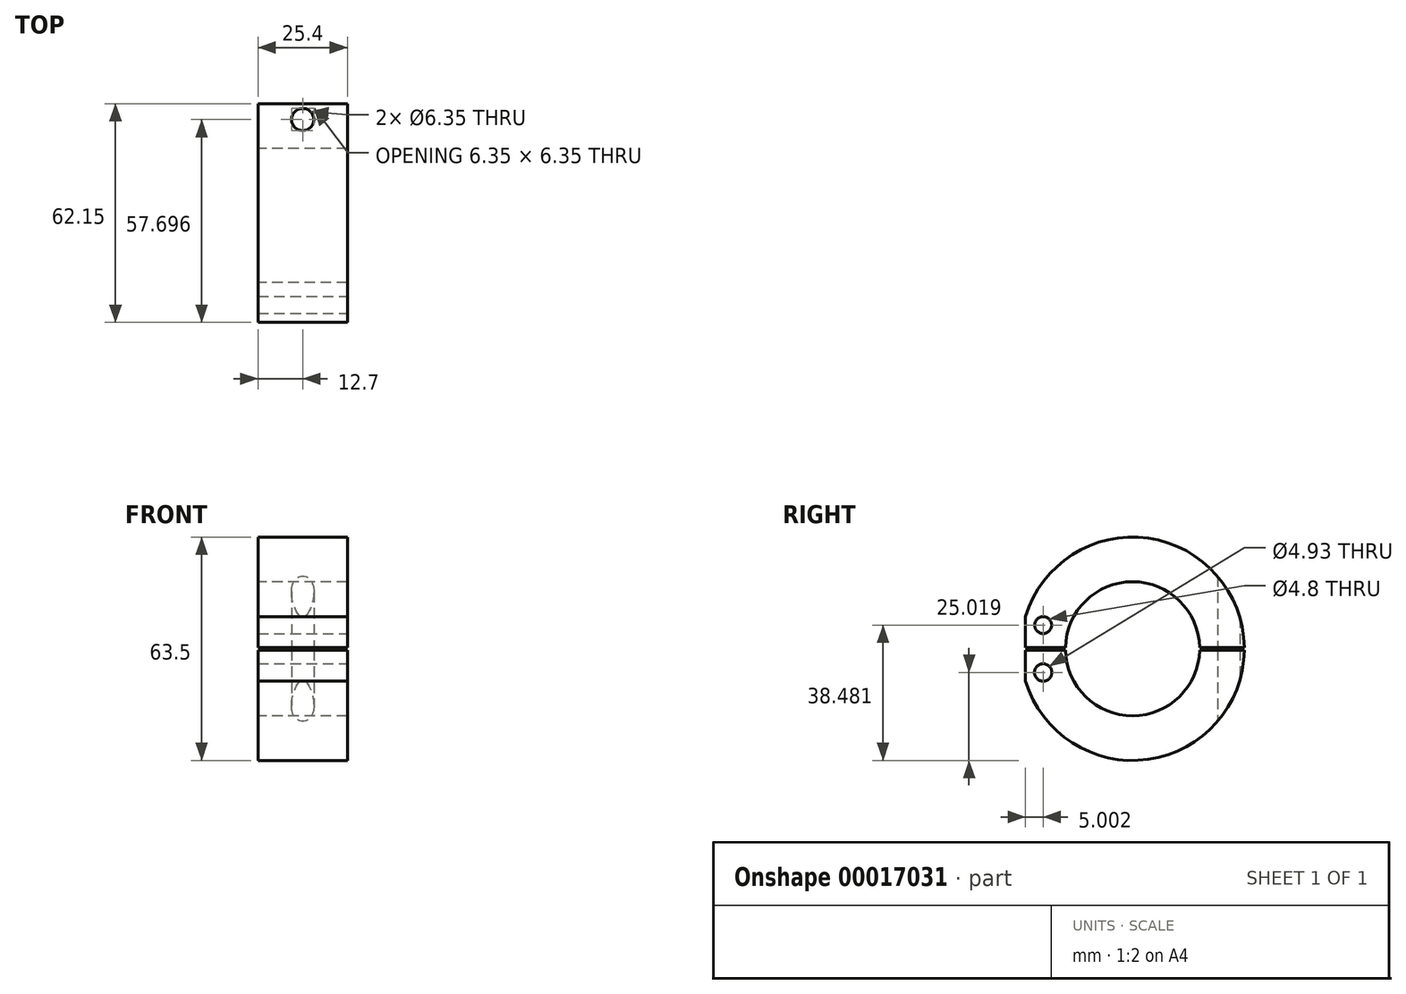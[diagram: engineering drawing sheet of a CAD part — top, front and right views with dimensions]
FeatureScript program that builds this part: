
annotation { "Feature Type Name" : "Feature", "Feature Type Description" : "" }
export const myFeature = defineFeature(function(context is Context, id is Id, definition is map)
    precondition{}
    {
        {
            var Q0;
            Q0=qCreatedBy(makeId("Right.planeOp"),FACE);
            var sketch = newSketch(context, id + "F0", { "sketchPlane" : qUnion([Q0])});
            skArc(sketch, "E0", {"start": v(-19.05, -0.38) * mm, "mid": v(0, -19.05) * mm, "end": v(19.05, -0.38) * mm});
            skArc(sketch, "E1", {"start": v(-31.75, -0.38) * mm, "mid": v(0, -31.75) * mm, "end": v(31.75, -0.38) * mm});
            skLineSegment(sketch, "E2.0", {"start": v(-31.75, 0.38) * mm, "end": v(-19.05, 0.38) * mm});
            skLineSegment(sketch, "E3.0", {"start": v(-31.75, -0.38) * mm, "end": v(-19.05, -0.38) * mm});
            skLineSegment(sketch, "E4.trimOffspring", {"start": v(19.05, 0.38) * mm, "end": v(31.75, 0.38) * mm});
            skArc(sketch, "E5.trimOffspring", {"start": v(19.05, 0.38) * mm, "mid": v(0, 19.05) * mm, "end": v(-19.05, 0.38) * mm});
            skArc(sketch, "E6.trimOffspring", {"start": v(31.75, 0.38) * mm, "mid": v(0, 31.75) * mm, "end": v(-31.75, 0.38) * mm});
            skLineSegment(sketch, "E7.trimOffspring", {"start": v(19.05, -0.38) * mm, "end": v(31.75, -0.38) * mm});
            skSolve(sketch);
        }
        {
            var Q0;
            Q0 = qSketchRegion(id + "F0", true);
            extrude(context, id + "F1", {"entities" : qUnion([Q0]), "depth" : 12.7 * mm, "hasSecondDirection" : true, "secondDirectionOppositeDirection" : true, "secondDirectionDepth" : 12.7 * mm});
        }
        {
            var Q0;
            Q0=qCreatedBy(makeId("Top.planeOp"),FACE);
            var sketch = newSketch(context, id + "F2", { "sketchPlane" : qUnion([Q0])});
            skCircle(sketch, "E8", {"center": v(0, 27.3) * mm, "radius": 3.18 * mm});
            skSolve(sketch);
        }
        {
            var Q0;
            Q0 = qSketchRegion(id + "F2", true);
            extrude(context, id + "F3", {"entities" : qUnion([Q0]), "operationType" : NewBodyOperationType.REMOVE, "depth" : 43.87 * mm, "hasSecondDirection" : true, "secondDirectionOppositeDirection" : true, "secondDirectionDepth" : 40.07 * mm});
        }
        {
            var Q0;
            Q0=makeQuery(id+"F1.opExtrude","CAP_FACE",FACE,{"disambiguationData":[OSD([sQuery(id+"F0.wireOp",EDGE,"E2.0"),sQuery(id+"F0.wireOp",EDGE,"E4.trimOffspring"),sQuery(id+"F0.wireOp",EDGE,"E5.trimOffspring"),sQuery(id+"F0.wireOp",EDGE,"E6.trimOffspring")])],"isStart":false});
            var sketch = newSketch(context, id + "F4", { "sketchPlane" : qUnion([Q0])});
            skCircle(sketch, "E9", {"center": v(-25.4, 6.73) * mm, "radius": 2.4 * mm});
            skCircle(sketch, "E10", {"center": v(-25.4, -6.73) * mm, "radius": 2.47 * mm});
            skSolve(sketch);
        }
        {
            var Q0;
            Q0=makeQuery(id+"F4.imprint","IMPRINT",FACE,{"disambiguationData":[TD([[makeQuery(id+"F4.imprint","IMPRINT",EDGE,{"derivedFrom":sQuery(id+"F4.wireOp",EDGE,"E9")}),1.0]])]});
            var Q1;
            Q1=makeQuery(id+"F4.imprint","IMPRINT",FACE,{"disambiguationData":[TD([[makeQuery(id+"F4.imprint","IMPRINT",EDGE,{"derivedFrom":sQuery(id+"F4.wireOp",EDGE,"E10")}),1.0]])]});
            extrude(context, id + "F5", {"entities" : qUnion([Q0, Q1]), "operationType" : NewBodyOperationType.REMOVE, "oppositeDirection" : true, "depth" : 36.73 * mm, "hasSecondDirection" : true, "secondDirectionOppositeDirection" : false, "secondDirectionDepth" : 38.42 * mm});
        }
        {
            var Q0;
            Q0=makeQuery(id+"F1.opExtrude","CAP_FACE",FACE,{"disambiguationData":[OSD([sQuery(id+"F0.wireOp",EDGE,"E0"),sQuery(id+"F0.wireOp",EDGE,"E1"),sQuery(id+"F0.wireOp",EDGE,"E3.0"),sQuery(id+"F0.wireOp",EDGE,"E7.trimOffspring")])],"isStart":false});
            var sketch = newSketch(context, id + "F6", { "sketchPlane" : qUnion([Q0])});
            skCircle(sketch, "E11", {"center": v(-25.4, -6.73) * mm, "radius": 2.37 * mm});
            skSolve(sketch);
        }
        {
            var Q0;
            Q0=makeQuery(id+"F6.imprint","IMPRINT",FACE,{"disambiguationData":[TD([[makeQuery(id+"F6.imprint","IMPRINT",EDGE,{"derivedFrom":sQuery(id+"F6.wireOp",EDGE,"E11")}),1.0]])]});
            extrude(context, id + "F7", {"entities" : qUnion([Q0]), "operationType" : NewBodyOperationType.REMOVE, "oppositeDirection" : true, "depth" : 25.4 * mm});
        }
        {
            var Q0;
            Q0=makeQuery(id+"F1.opExtrude","CAP_FACE",FACE,{"disambiguationData":[OSD([sQuery(id+"F0.wireOp",EDGE,"E2.0"),sQuery(id+"F0.wireOp",EDGE,"E4.trimOffspring"),sQuery(id+"F0.wireOp",EDGE,"E5.trimOffspring"),sQuery(id+"F0.wireOp",EDGE,"E6.trimOffspring")])],"isStart":true});
            var sketch = newSketch(context, id + "F8", { "sketchPlane" : qUnion([Q0])});
            skLineSegment(sketch, "E12", {"start": v(32.68, 10.3) * mm, "end": v(32.68, -15.37) * mm});
            skLineSegment(sketch, "E13", {"start": v(32.82, -15.22) * mm, "end": v(30.4, -15.22) * mm});
            skLineSegment(sketch, "E14", {"start": v(30.4, -15.22) * mm, "end": v(30.4, 12.08) * mm});
            skLineSegment(sketch, "E15", {"start": v(30.4, 12.08) * mm, "end": v(32.68, 10.3) * mm});
            skSolve(sketch);
        }
        {
            var Q0;
            Q0 = qSketchRegion(id + "F8", true);
            extrude(context, id + "F9", {"entities" : qUnion([Q0]), "operationType" : NewBodyOperationType.REMOVE, "oppositeDirection" : true, "depth" : 25.4 * mm});
        }
    });
